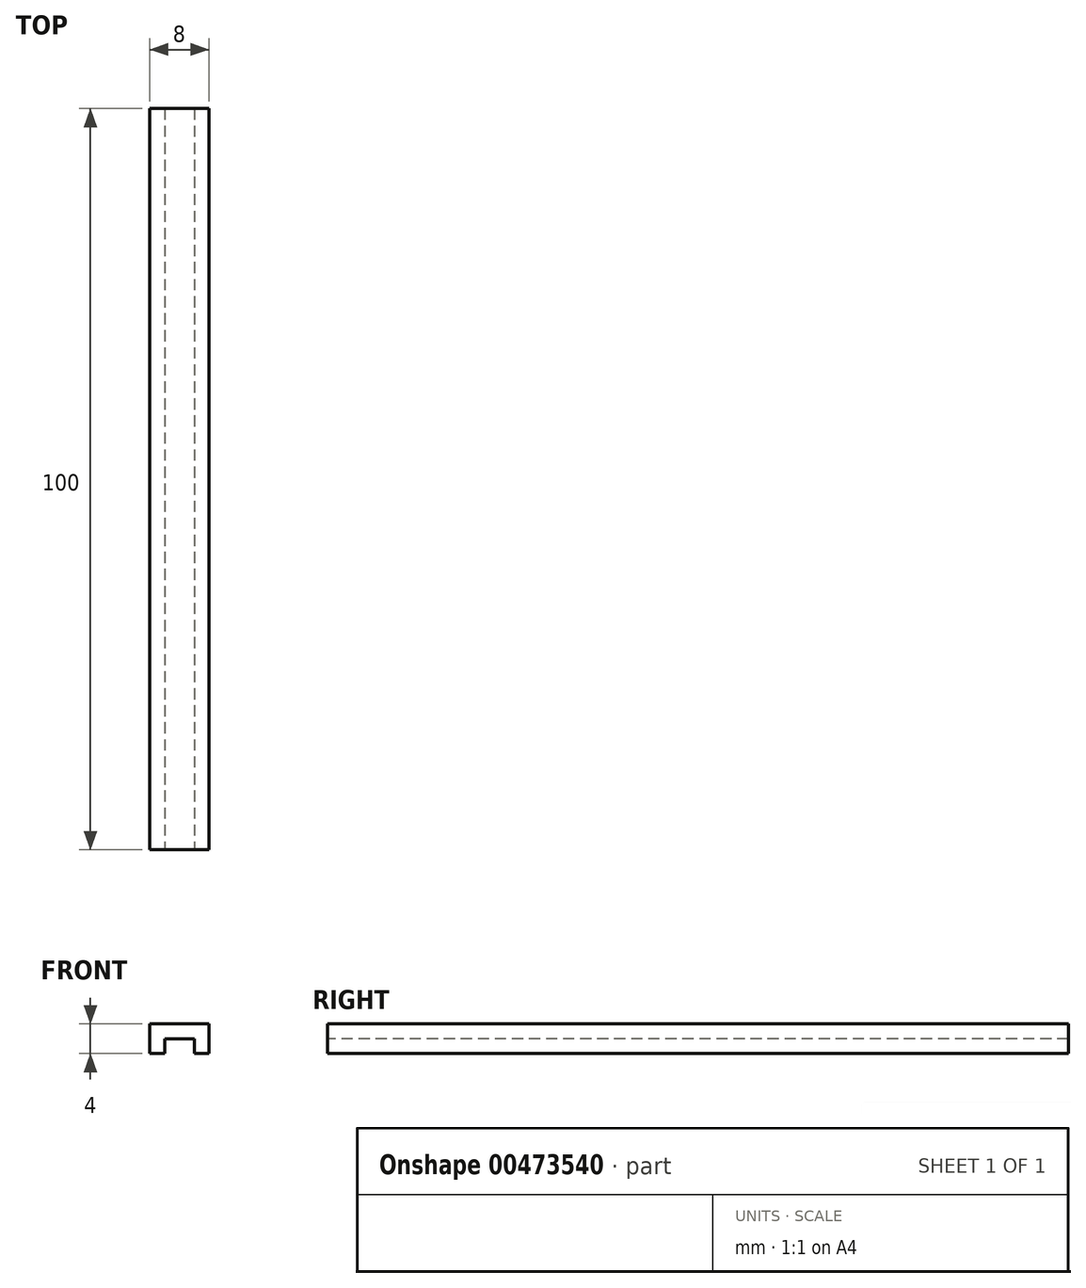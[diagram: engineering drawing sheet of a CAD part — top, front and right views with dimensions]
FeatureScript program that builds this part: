
annotation { "Feature Type Name" : "Feature", "Feature Type Description" : "" }
export const myFeature = defineFeature(function(context is Context, id is Id, definition is map)
    precondition{}
    {
        {
            var Q0;
            Q0=qCreatedBy(makeId("Top.planeOp"),FACE);
            var sketch = newSketch(context, id + "F0", { "sketchPlane" : qUnion([Q0])});
            skLineSegment(sketch, "E0.bottom", {"start": v(4, 50) * mm, "end": v(-4, 50) * mm});
            skLineSegment(sketch, "E0.top", {"start": v(4, -50) * mm, "end": v(-4, -50) * mm});
            skLineSegment(sketch, "E0.left", {"start": v(4, 50) * mm, "end": v(4, -50) * mm});
            skLineSegment(sketch, "E0.right", {"start": v(-4, 50) * mm, "end": v(-4, -50) * mm});
            skPoint(sketch, "E0.middle", {"position": v(0, 0) * mm});
            skSolve(sketch);
        }
        {
            var Q0;
            Q0=qCreatedBy(makeId("Top.planeOp"),FACE);
            var sketch = newSketch(context, id + "F1", { "sketchPlane" : qUnion([Q0])});
            skLineSegment(sketch, "E1.bottom", {"start": v(2, 75) * mm, "end": v(-2, 75) * mm});
            skLineSegment(sketch, "E1.top", {"start": v(2, -75) * mm, "end": v(-2, -75) * mm});
            skLineSegment(sketch, "E1.left", {"start": v(2, 75) * mm, "end": v(2, -75) * mm});
            skLineSegment(sketch, "E1.right", {"start": v(-2, 75) * mm, "end": v(-2, -75) * mm});
            skPoint(sketch, "E1.middle", {"position": v(0, 0) * mm});
            skSolve(sketch);
        }
        {
            var Q0;
            Q0 = qSketchRegion(id + "F0", true);
            extrude(context, id + "F2", {"entities" : qUnion([Q0]), "depth" : 4 * mm});
        }
        {
            var Q0;
            Q0 = qSketchRegion(id + "F1", true);
            extrude(context, id + "F3", {"entities" : qUnion([Q0]), "operationType" : NewBodyOperationType.REMOVE, "depth" : 2 * mm});
        }
    });
